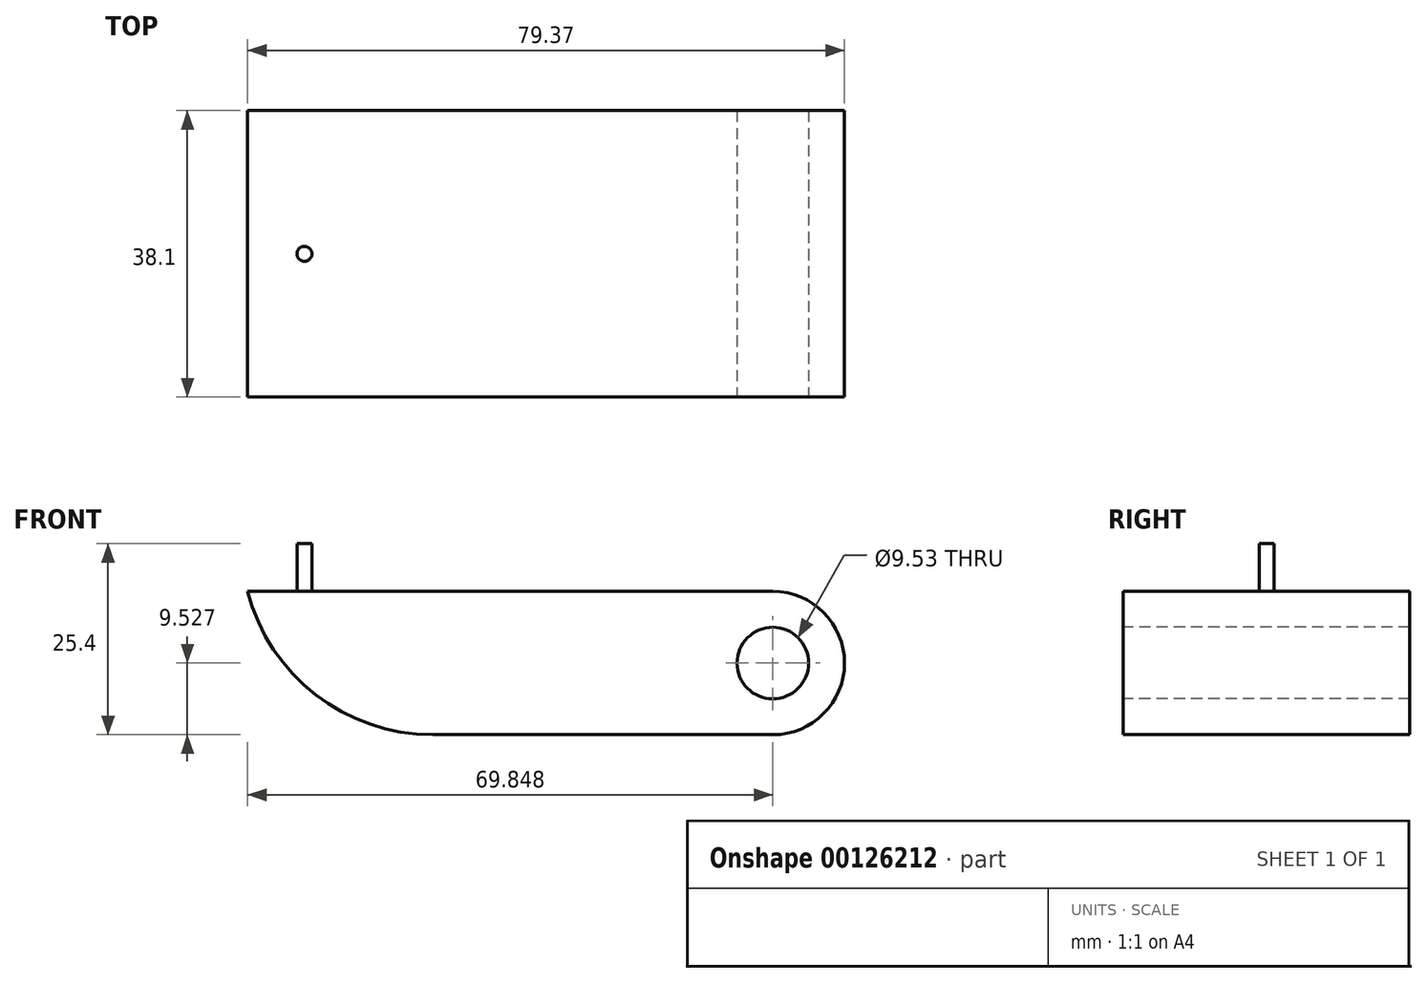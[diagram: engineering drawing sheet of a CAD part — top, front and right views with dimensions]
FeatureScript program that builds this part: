
annotation { "Feature Type Name" : "Feature", "Feature Type Description" : "" }
export const myFeature = defineFeature(function(context is Context, id is Id, definition is map)
    precondition{}
    {
        {
            var Q0;
            Q0=qCreatedBy(makeId("Front.planeOp"),FACE);
            var sketch = newSketch(context, id + "F0", { "sketchPlane" : qUnion([Q0])});
            skLineSegment(sketch, "E0", {"start": v(-32.5, 5.93) * mm, "end": v(37.35, 5.93) * mm});
            skLineSegment(sketch, "E1", {"start": v(-32.5, -13.12) * mm, "end": v(37.35, -13.12) * mm});
            skArc(sketch, "E2", {"start": v(37.35, -13.12) * mm, "mid": v(46.87, -3.6) * mm, "end": v(37.35, 5.93) * mm});
            skLineSegment(sketch, "E3", {"start": v(-32.5, 5.93) * mm, "end": v(-32.5, -13.12) * mm});
            skSolve(sketch);
        }
        {
            var Q0;
            Q0=makeQuery(id+"F0.imprint","IMPRINT",FACE,{"disambiguationData":[TD([[makeQuery(id+"F0.imprint","IMPRINT",EDGE,{"derivedFrom":sQuery(id+"F0.wireOp",EDGE,"E0")}),-1.0]])]});
            extrude(context, id + "F1", {"entities" : qUnion([Q0]), "depth" : 38.1 * mm});
        }
        {
            var Q0;
            Q0=makeQuery(id+"F1.opExtrude","SWEPT_EDGE",EDGE,{"disambiguationData":[OSD([sQuery(id+"F0.wireOp",EDGE,"E1"),sQuery(id+"F0.wireOp",EDGE,"E3")])]});
            fillet(context, id + "F2", {"entities" : qUnion([Q0]), "radius" : 25.4 * mm, "tangentPropagation" : true, "allowEdgeOverflow" : false});
        }
        {
            var Q0;
            Q0=makeQuery(id+"F1.opExtrude","CAP_FACE",FACE,{"disambiguationData":[OSD([sQuery(id+"F0.wireOp",EDGE,"E0"),sQuery(id+"F0.wireOp",EDGE,"E1"),sQuery(id+"F0.wireOp",EDGE,"E2"),sQuery(id+"F0.wireOp",EDGE,"E3")])],"isStart":false});
            var sketch = newSketch(context, id + "F3", { "sketchPlane" : qUnion([Q0])});
            skPoint(sketch, "E4", {"position": v(37.35, -3.6) * mm});
            skSolve(sketch);
        }
        {
            var Q0;
            Q0=sQuery(id+"F3.wireOp",VERTEX,"E4");
            var Q1;
            Q1=makeQuery(id+"F1.opExtrude","SWEPT_BODY",BODY,{"disambiguationData":[OSD([sQuery(id+"F0.wireOp",EDGE,"E0"),sQuery(id+"F0.wireOp",EDGE,"E1"),sQuery(id+"F0.wireOp",EDGE,"E2"),sQuery(id+"F0.wireOp",EDGE,"E3")])]});
            hole(context, id + "F4", {"style" : HoleStyle.SIMPLE, "endStyle" : HoleEndStyle.THROUGH, "holeDiameter" : 9.52 * mm, "locations" : qUnion([Q0]), "scope" : qUnion([Q1]), "isTappedThrough" : true});
        }
        {
            var Q0;
            Q0=makeQuery(id+"F1.opExtrude","SWEPT_FACE",FACE,{"disambiguationData":[OSD([sQuery(id+"F0.wireOp",EDGE,"E0")])]});
            var sketch = newSketch(context, id + "F5", { "sketchPlane" : qUnion([Q0])});
            skPoint(sketch, "E5.positionSnap0", {"position": v(-32.5, -19.05) * mm});
            skCircle(sketch, "E6", {"center": v(-24.95, -19.05) * mm, "radius": 1 * mm});
            skSolve(sketch);
        }
        {
            var Q0;
            Q0=makeQuery(id+"F5.imprint","IMPRINT",FACE,{"disambiguationData":[TD([[makeQuery(id+"F5.imprint","IMPRINT",EDGE,{"derivedFrom":sQuery(id+"F5.wireOp",EDGE,"E6")}),1.0]])]});
            extrude(context, id + "F6", {"entities" : qUnion([Q0]), "operationType" : NewBodyOperationType.ADD, "depth" : 6.35 * mm});
        }
    });
